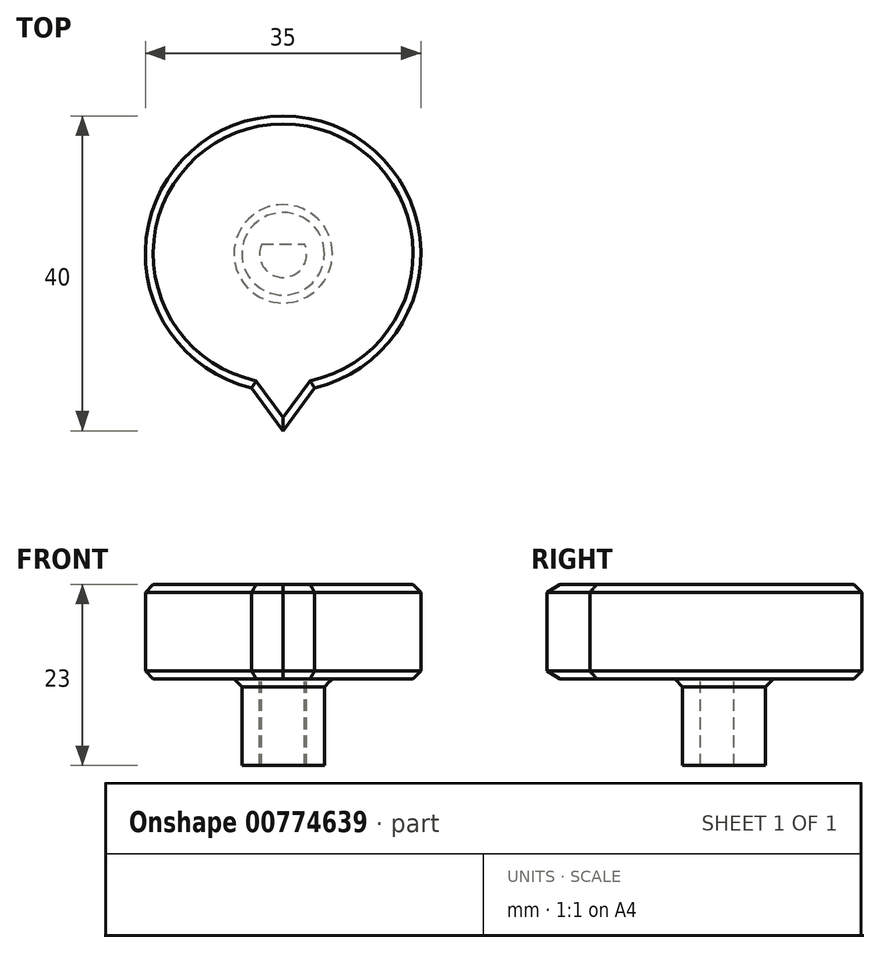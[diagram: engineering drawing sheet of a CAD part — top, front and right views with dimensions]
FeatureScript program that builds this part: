
annotation { "Feature Type Name" : "Feature", "Feature Type Description" : "" }
export const myFeature = defineFeature(function(context is Context, id is Id, definition is map)
    precondition{}
    {
        {
            var Q0;
            Q0=qCreatedBy(makeId("Top.planeOp"),FACE);
            var sketch = newSketch(context, id + "F0", { "sketchPlane" : qUnion([Q0])});
            skCircle(sketch, "E0", {"center": v(0, 0) * mm, "radius": 17.5 * mm});
            skCircle(sketch, "E1", {"center": v(0, 0) * mm, "radius": 5.25 * mm});
            skCircle(sketch, "E2", {"center": v(0, 0) * mm, "radius": 3 * mm});
            skLineSegment(sketch, "E3", {"start": v(-2.73, 1.25) * mm, "end": v(2.73, 1.25) * mm});
            skLineSegment(sketch, "E4", {"start": v(0, -22.5) * mm, "end": v(4, -17.04) * mm});
            skLineSegment(sketch, "E5", {"start": v(0, -22.5) * mm, "end": v(-4, -17.04) * mm});
            skSolve(sketch);
        }
        {
            var Q0;
            Q0=makeQuery(id+"F0.imprint","IMPRINT",FACE,{"disambiguationData":[TD([[makeQuery(id+"F0.imprint","IMPRINT",EDGE,{"derivedFrom":sQuery(id+"F0.wireOp",EDGE,"E0")}),1.0]])]});
            var Q1;
            Q1=makeQuery(id+"F0.imprint","IMPRINT",FACE,{"disambiguationData":[TD([[makeQuery(id+"F0.imprint","IMPRINT",EDGE,{"derivedFrom":sQuery(id+"F0.wireOp",EDGE,"E1")}),1.0]])]});
            var Q2;
            {var subQ0=sQuery(id+"F0.wireOp",EDGE,"E3");Q2=makeQuery(id+"F0.imprint","IMPRINT",FACE,{"disambiguationData":[TD([[makeQuery(id+"F0.imprint","IMPRINT",EDGE,{"derivedFrom":subQ0}),-1.0]])]});}
            var Q3;
            {var subQ0=sQuery(id+"F0.wireOp",EDGE,"E3");Q3=makeQuery(id+"F0.imprint","IMPRINT",FACE,{"disambiguationData":[TD([[makeQuery(id+"F0.imprint","IMPRINT",EDGE,{"derivedFrom":subQ0}),1.0]])]});}
            extrude(context, id + "F1", {"entities" : qUnion([Q0, Q1, Q2, Q3]), "depth" : 12 * mm, "offsetDistance" : 25 * mm});
        }
        {
            var Q0;
            Q0=makeQuery(id+"F0.imprint","IMPRINT",FACE,{"disambiguationData":[TD([[makeQuery(id+"F0.imprint","IMPRINT",EDGE,{"derivedFrom":sQuery(id+"F0.wireOp",EDGE,"E1")}),1.0]])]});
            var Q1;
            {var subQ0=sQuery(id+"F0.wireOp",EDGE,"E3");Q1=makeQuery(id+"F0.imprint","IMPRINT",FACE,{"disambiguationData":[TD([[makeQuery(id+"F0.imprint","IMPRINT",EDGE,{"derivedFrom":subQ0}),1.0]])]});}
            extrude(context, id + "F2", {"entities" : qUnion([Q0, Q1]), "operationType" : NewBodyOperationType.ADD, "oppositeDirection" : true, "depth" : 11 * mm, "offsetDistance" : 25 * mm});
        }
        {
            var Q0;
            {var subQ0=sQuery(id+"F0.wireOp",EDGE,"E4");Q0=makeQuery(id+"F0.imprint","IMPRINT",FACE,{"disambiguationData":[TD([[makeQuery(id+"F0.imprint","IMPRINT",EDGE,{"derivedFrom":subQ0}),1.0]])]});}
            extrude(context, id + "F3", {"entities" : qUnion([Q0]), "operationType" : NewBodyOperationType.ADD, "depth" : 12 * mm, "offsetDistance" : 25 * mm});
        }
        {
            var Q0;
            {var subQ0=sQuery(id+"F0.wireOp",EDGE,"E0");Q0=makeQuery(id+"F3.boolean.opBoolean","MERGE",FACE,{"derivedFrom":[makeQuery(id+"F2.boolean.opBoolean","SPLIT",FACE,{"disambiguationData":[TD([makeQuery(id+"F1.opExtrude","SWEPT_FACE",FACE,{"disambiguationData":[OSD([subQ0])]})])],"derivedFrom":makeQuery(id+"F1.opExtrude","CAP_FACE",FACE,{"disambiguationData":[OSD([subQ0])],"isStart":true})}),makeQuery(id+"F3.opExtrude","CAP_FACE",FACE,{"disambiguationData":[OSD([subQ0,sQuery(id+"F0.wireOp",EDGE,"E4"),sQuery(id+"F0.wireOp",EDGE,"E5")])],"isStart":true})]});}
            chamfer(context, id + "F4", {"entities" : qUnion([Q0]), "width" : 1 * mm, "tangentPropagation" : true});
        }
        {
            var Q0;
            {var subQ0=sQuery(id+"F0.wireOp",EDGE,"E0");Q0=makeQuery(id+"F3.boolean.opBoolean","MERGE",FACE,{"derivedFrom":[makeQuery(id+"F1.opExtrude","CAP_FACE",FACE,{"disambiguationData":[OSD([subQ0])],"isStart":false}),makeQuery(id+"F3.opExtrude","CAP_FACE",FACE,{"disambiguationData":[OSD([subQ0,sQuery(id+"F0.wireOp",EDGE,"E4"),sQuery(id+"F0.wireOp",EDGE,"E5")])],"isStart":false})]});}
            chamfer(context, id + "F5", {"entities" : qUnion([Q0]), "width" : 1 * mm, "tangentPropagation" : true});
        }
    });
